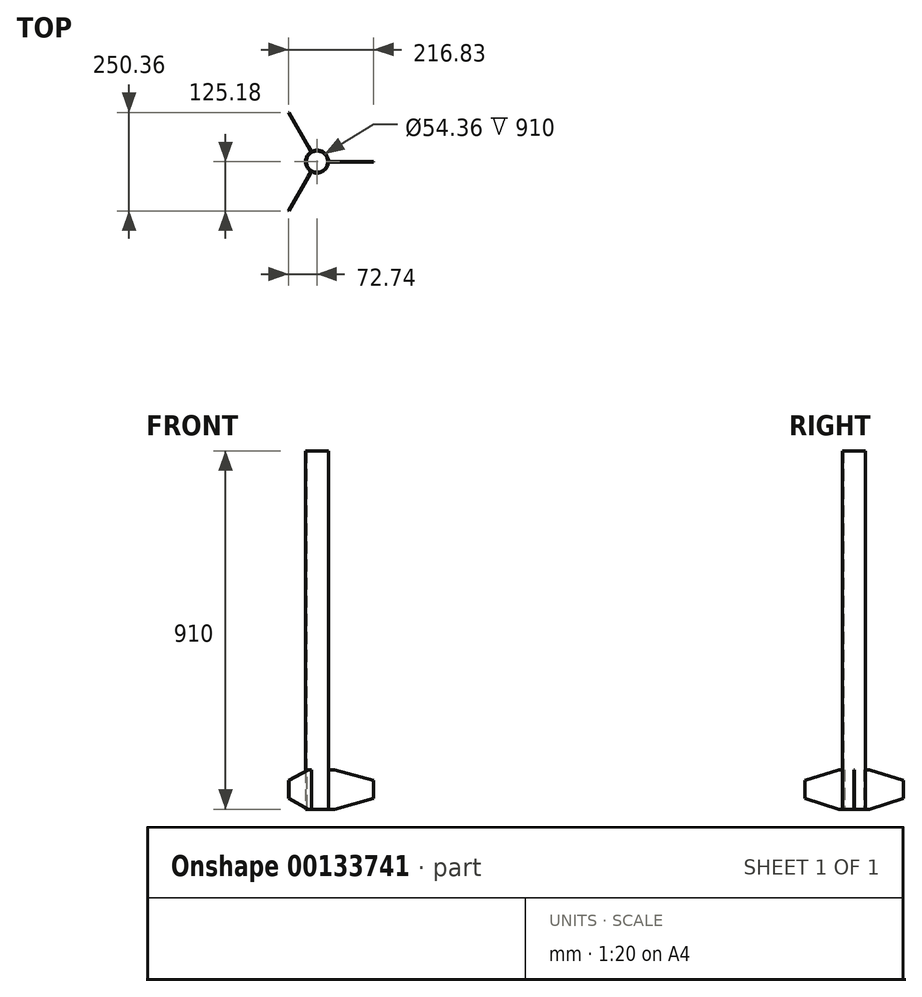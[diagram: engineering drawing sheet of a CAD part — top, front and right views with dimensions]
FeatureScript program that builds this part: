
annotation { "Feature Type Name" : "Feature", "Feature Type Description" : "" }
export const myFeature = defineFeature(function(context is Context, id is Id, definition is map)
    precondition{}
    {
        {
            var Q0;
            Q0=qCreatedBy(makeId("Top.planeOp"),FACE);
            var sketch = newSketch(context, id + "F0", { "sketchPlane" : qUnion([Q0])});
            skCircle(sketch, "E0", {"center": v(0, 0) * mm, "radius": 29.1 * mm});
            skCircle(sketch, "E1", {"center": v(0, 0) * mm, "radius": 27.18 * mm});
            skLineSegment(sketch, "E2", {"start": v(29.09, 0.8) * mm, "end": v(144.09, 0.8) * mm});
            skLineSegment(sketch, "E3", {"start": v(144.09, 0.8) * mm, "end": v(144.09, -0.8) * mm});
            skLineSegment(sketch, "E4", {"start": v(144.09, -0.8) * mm, "end": v(29.09, -0.8) * mm});
            skPoint(sketch, "E5", {"position": v(144.09, 0) * mm});
            skLineSegment(sketch, "E6.1.0", {"start": v(-15.24, 24.8) * mm, "end": v(-72.74, 124.38) * mm});
            skLineSegment(sketch, "E6.1.1", {"start": v(-71.35, 125.18) * mm, "end": v(-13.85, 25.6) * mm});
            skLineSegment(sketch, "E6.1.2", {"start": v(-72.74, 124.38) * mm, "end": v(-71.35, 125.18) * mm});
            skLineSegment(sketch, "E6.2.0", {"start": v(-13.85, -25.6) * mm, "end": v(-71.35, -125.18) * mm});
            skLineSegment(sketch, "E6.2.1", {"start": v(-72.74, -124.38) * mm, "end": v(-15.24, -24.8) * mm});
            skLineSegment(sketch, "E6.2.2", {"start": v(-71.35, -125.18) * mm, "end": v(-72.74, -124.38) * mm});
            skSolve(sketch);
        }
        {
            var Q0;
            Q0=makeQuery(id+"F0.imprint","IMPRINT",FACE,{"disambiguationData":[TD([[makeQuery(id+"F0.imprint","IMPRINT",EDGE,{"derivedFrom":sQuery(id+"F0.wireOp",EDGE,"E0")}),1.0]])]});
            extrude(context, id + "F1", {"entities" : qUnion([Q0]), "depth" : 910 * mm});
        }
        {
            var Q0;
            {var subQ0=sQuery(id+"F0.wireOp",EDGE,"E2");Q0=makeQuery(id+"F0.imprint","IMPRINT",FACE,{"disambiguationData":[TD([[makeQuery(id+"F0.imprint","IMPRINT",EDGE,{"derivedFrom":subQ0}),-1.0]])]});}
            var Q1;
            {var subQ0=sQuery(id+"F0.wireOp",EDGE,"E6.2.0");Q1=makeQuery(id+"F0.imprint","IMPRINT",FACE,{"disambiguationData":[TD([[makeQuery(id+"F0.imprint","IMPRINT",EDGE,{"derivedFrom":subQ0}),-1.0]])]});}
            var Q2;
            {var subQ0=sQuery(id+"F0.wireOp",EDGE,"E6.1.0");Q2=makeQuery(id+"F0.imprint","IMPRINT",FACE,{"disambiguationData":[TD([[makeQuery(id+"F0.imprint","IMPRINT",EDGE,{"derivedFrom":subQ0}),-1.0]])]});}
            extrude(context, id + "F2", {"entities" : qUnion([Q0, Q1, Q2]), "operationType" : NewBodyOperationType.ADD, "depth" : 100 * mm});
        }
        {
            var Q0;
            Q0=makeQuery(id+"F2.opExtrude","CAP_EDGE",EDGE,{"disambiguationData":[OSD([sQuery(id+"F0.wireOp",EDGE,"E6.2.2")])],"isStart":false});
            var Q1;
            Q1=makeQuery(id+"F2.opExtrude","CAP_EDGE",EDGE,{"disambiguationData":[OSD([sQuery(id+"F0.wireOp",EDGE,"E3")])],"isStart":false});
            var Q2;
            Q2=makeQuery(id+"F2.opExtrude","CAP_EDGE",EDGE,{"disambiguationData":[OSD([sQuery(id+"F0.wireOp",EDGE,"E6.1.2")])],"isStart":false});
            chamfer(context, id + "F3", {"entities" : qUnion([Q0, Q1, Q2]), "chamferType" : ChamferType.TWO_OFFSETS, "width1" : 27 * mm, "oppositeDirection" : false, "width2" : 100 * mm, "tangentPropagation" : true});
        }
        {
            var Q0;
            Q0=makeQuery(id+"F2.opExtrude","CAP_EDGE",EDGE,{"disambiguationData":[OSD([sQuery(id+"F0.wireOp",EDGE,"E3")])],"isStart":true});
            var Q1;
            Q1=makeQuery(id+"F2.opExtrude","CAP_EDGE",EDGE,{"disambiguationData":[OSD([sQuery(id+"F0.wireOp",EDGE,"E6.1.2")])],"isStart":true});
            var Q2;
            Q2=makeQuery(id+"F2.opExtrude","CAP_EDGE",EDGE,{"disambiguationData":[OSD([sQuery(id+"F0.wireOp",EDGE,"E6.2.2")])],"isStart":true});
            chamfer(context, id + "F4", {"entities" : qUnion([Q0, Q1, Q2]), "chamferType" : ChamferType.TWO_OFFSETS, "width1" : 100 * mm, "oppositeDirection" : false, "width2" : 27 * mm, "tangentPropagation" : true});
        }
    });
